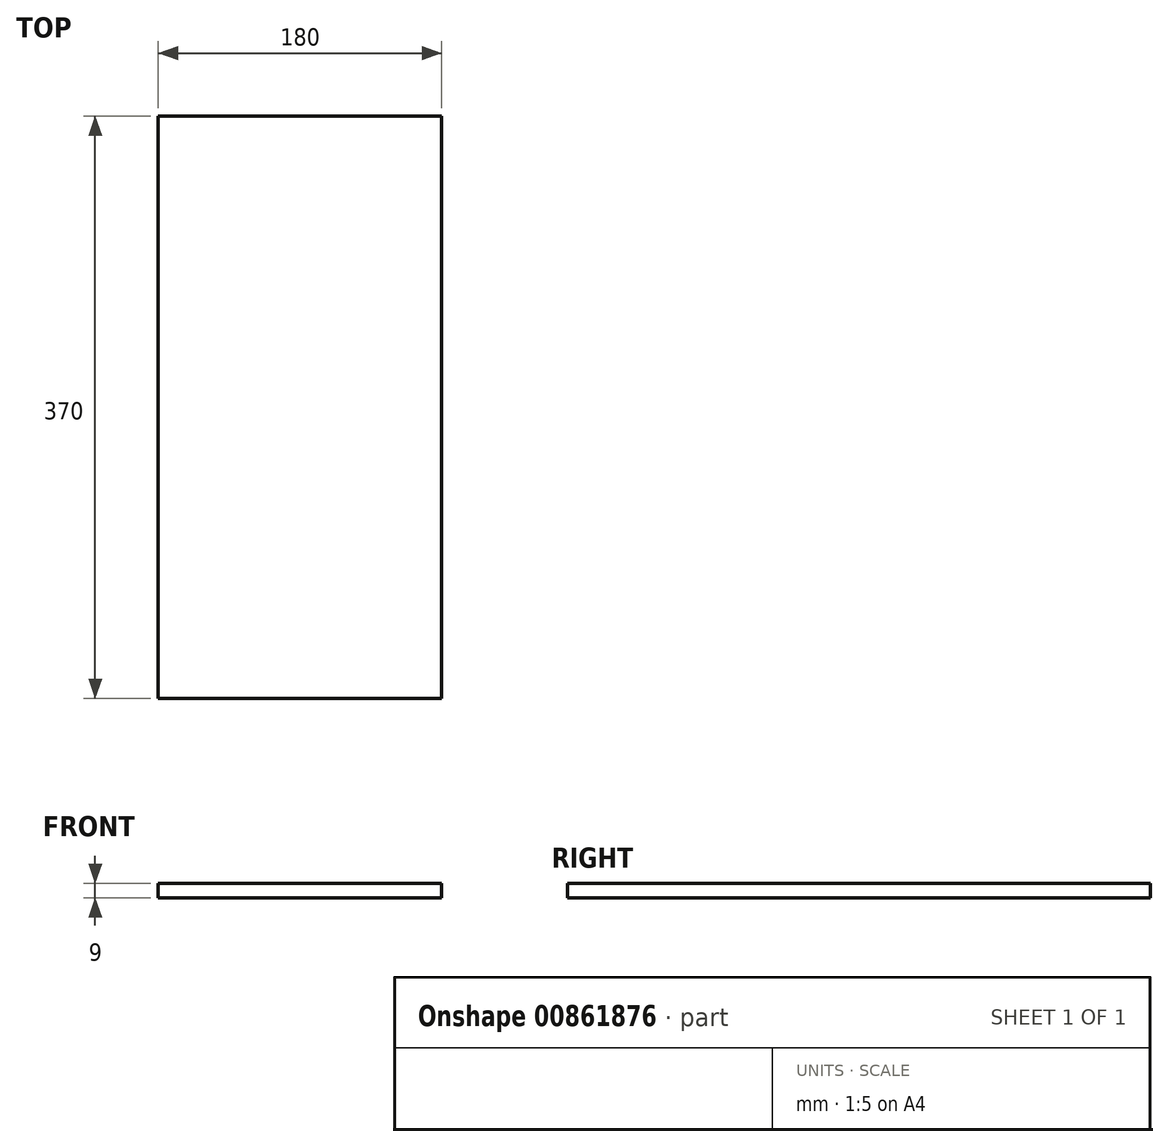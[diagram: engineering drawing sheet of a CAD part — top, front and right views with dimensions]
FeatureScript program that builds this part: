
annotation { "Feature Type Name" : "Feature", "Feature Type Description" : "" }
export const myFeature = defineFeature(function(context is Context, id is Id, definition is map)
    precondition{}
    {
        {
            var Q0;
            Q0=qCreatedBy(makeId("Top.planeOp"),FACE);
            var sketch = newSketch(context, id + "F0", { "sketchPlane" : qUnion([Q0])});
            skLineSegment(sketch, "E0.bottom", {"start": v(90, 185) * mm, "end": v(-90, 185) * mm});
            skLineSegment(sketch, "E0.top", {"start": v(90, -185) * mm, "end": v(-90, -185) * mm});
            skLineSegment(sketch, "E0.left", {"start": v(90, 185) * mm, "end": v(90, -185) * mm});
            skLineSegment(sketch, "E0.right", {"start": v(-90, 185) * mm, "end": v(-90, -185) * mm});
            skPoint(sketch, "E0.middle", {"position": v(0, 0) * mm});
            skSolve(sketch);
        }
        {
            var Q0;
            Q0 = qSketchRegion(id + "F0", true);
            extrude(context, id + "F1", {"entities" : qUnion([Q0]), "depth" : 9 * mm, "offsetDistance" : 25 * mm});
        }
    });
